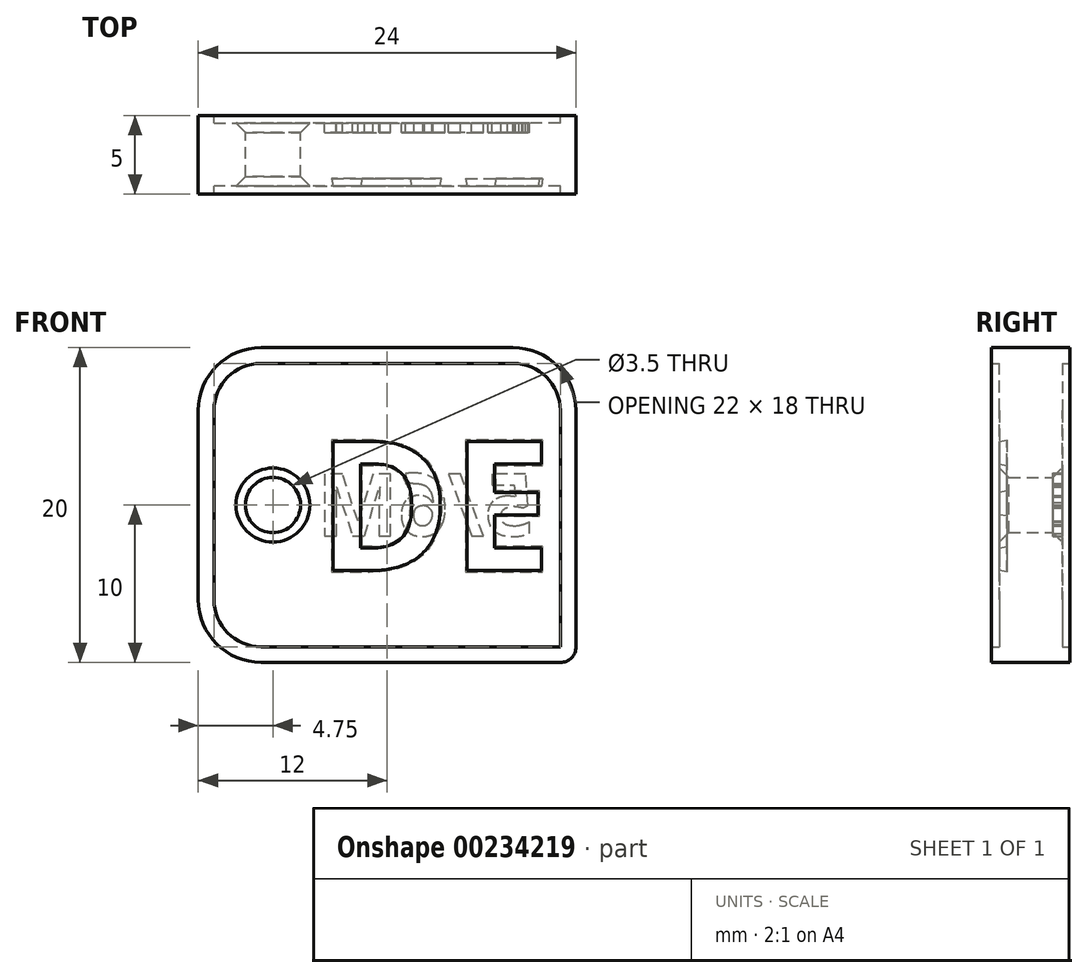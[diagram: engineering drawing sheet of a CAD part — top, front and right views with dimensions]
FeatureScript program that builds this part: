
annotation { "Feature Type Name" : "Feature", "Feature Type Description" : "" }
export const myFeature = defineFeature(function(context is Context, id is Id, definition is map)
    precondition{}
    {
        {
            var Q0;
            Q0=qCreatedBy(makeId("Front.planeOp"),FACE);
            var sketch = newSketch(context, id + "F0", { "sketchPlane" : qUnion([Q0])});
            skLineSegment(sketch, "E0.bottom", {"start": v(12, -10) * mm, "end": v(-12, -10) * mm});
            skLineSegment(sketch, "E0.top", {"start": v(12, 10) * mm, "end": v(-12, 10) * mm});
            skLineSegment(sketch, "E0.left", {"start": v(12, -10) * mm, "end": v(12, 10) * mm});
            skLineSegment(sketch, "E0.right", {"start": v(-12, -10) * mm, "end": v(-12, 10) * mm});
            skPoint(sketch, "E0.middle", {"position": v(0, 0) * mm});
            skCircle(sketch, "E1", {"center": v(-7.25, 0) * mm, "radius": 1.75 * mm});
            skSolve(sketch);
        }
        {
            var Q0;
            Q0=qSketchRegion(id+"F0",true);
            extrude(context, id + "F1", {"entities" : qUnion([Q0]), "endBound" : BoundingType.SYMMETRIC, "depth" : 4 * mm});
        }
        {
            var Q0;
            Q0=makeQuery(id+"F1.opExtrude","SWEPT_EDGE",EDGE,{"disambiguationData":[OSD([sQuery(id+"F0.wireOp",EDGE,"E0.top"),sQuery(id+"F0.wireOp",EDGE,"E0.right")])]});
            var Q1;
            Q1=makeQuery(id+"F1.opExtrude","SWEPT_EDGE",EDGE,{"disambiguationData":[OSD([sQuery(id+"F0.wireOp",EDGE,"E0.top"),sQuery(id+"F0.wireOp",EDGE,"E0.left")])]});
            var Q2;
            Q2=makeQuery(id+"F1.opExtrude","SWEPT_EDGE",EDGE,{"disambiguationData":[OSD([sQuery(id+"F0.wireOp",EDGE,"E0.bottom"),sQuery(id+"F0.wireOp",EDGE,"E0.right")])]});
            fillet(context, id + "F2", {"entities" : qUnion([Q0, Q1, Q2]), "radius" : 4 * mm, "tangentPropagation" : true, "allowEdgeOverflow" : false});
        }
        {
            var Q0;
            Q0=makeQuery(id+"F1.opExtrude","SWEPT_EDGE",EDGE,{"disambiguationData":[OSD([sQuery(id+"F0.wireOp",EDGE,"E0.bottom"),sQuery(id+"F0.wireOp",EDGE,"E0.left")])]});
            fillet(context, id + "F3", {"entities" : qUnion([Q0]), "radius" : 1 * mm, "tangentPropagation" : true, "allowEdgeOverflow" : false});
        }
        {
            var Q0;
            Q0=qCreatedBy(makeId("Front.planeOp"),FACE);
            var sketch = newSketch(context, id + "F4", { "sketchPlane" : qUnion([Q0])});
            skArc(sketch, "E2.0", {"start": v(-11, -6) * mm, "mid": v(-10.12, -8.12) * mm, "end": v(-8, -9) * mm});
            skLineSegment(sketch, "E2.1", {"start": v(-11, 6) * mm, "end": v(-11, -6) * mm});
            skLineSegment(sketch, "E2.2", {"start": v(11, -9) * mm, "end": v(11, 6) * mm});
            skArc(sketch, "E2.3", {"start": v(11, 6) * mm, "mid": v(10.12, 8.12) * mm, "end": v(8, 9) * mm});
            skLineSegment(sketch, "E2.4", {"start": v(8, 9) * mm, "end": v(-8, 9) * mm});
            skLineSegment(sketch, "E2.5", {"start": v(-8, -9) * mm, "end": v(11, -9) * mm});
            skArc(sketch, "E2.6", {"start": v(-8, 9) * mm, "mid": v(-10.12, 8.12) * mm, "end": v(-11, 6) * mm});
            skArc(sketch, "E3.0", {"start": v(-12, -6) * mm, "mid": v(-10.83, -8.83) * mm, "end": v(-8, -10) * mm});
            skLineSegment(sketch, "E3.1", {"start": v(-12, 6) * mm, "end": v(-12, -6) * mm});
            skLineSegment(sketch, "E3.2", {"start": v(-8, -10) * mm, "end": v(11, -10) * mm});
            skArc(sketch, "E3.3", {"start": v(-8, 10) * mm, "mid": v(-10.83, 8.83) * mm, "end": v(-12, 6) * mm});
            skArc(sketch, "E3.4", {"start": v(11, -10) * mm, "mid": v(11.7, -9.7) * mm, "end": v(12, -9) * mm});
            skLineSegment(sketch, "E3.5", {"start": v(12, -9) * mm, "end": v(12, 6) * mm});
            skArc(sketch, "E3.6", {"start": v(12, 6) * mm, "mid": v(10.83, 8.83) * mm, "end": v(8, 10) * mm});
            skLineSegment(sketch, "E3.7", {"start": v(8, 10) * mm, "end": v(-8, 10) * mm});
            skSolve(sketch);
        }
        {
            var Q0;
            Q0=qSketchRegion(id+"F4",true);
            extrude(context, id + "F5", {"entities" : qUnion([Q0]), "operationType" : NewBodyOperationType.ADD, "endBound" : BoundingType.SYMMETRIC, "depth" : 5 * mm});
        }
        {
            var Q0;
            Q0=makeQuery(id+"F1.opExtrude","CAP_FACE",FACE,{"disambiguationData":[OSD([sQuery(id+"F0.wireOp",EDGE,"E0.bottom"),sQuery(id+"F0.wireOp",EDGE,"E0.top"),sQuery(id+"F0.wireOp",EDGE,"E0.left"),sQuery(id+"F0.wireOp",EDGE,"E0.right"),sQuery(id+"F0.wireOp",EDGE,"E1")])],"isStart":false});
            var sketch = newSketch(context, id + "F6", { "sketchPlane" : qUnion([Q0])});
            skText(sketch, "E4", { "text": "DE", "fontName": "OpenSans-Bold.ttf"});
            const initialGuessF6  = {"E4": [-0.00446, -0.00417, 1, 0, 0.00827]};
            skSetInitialGuess(sketch, initialGuessF6);
            skSolve(sketch);
        }
        {
            var Q0;
            Q0=qSketchRegion(id+"F6",true);
            extrude(context, id + "F7", {"entities" : qUnion([Q0]), "operationType" : NewBodyOperationType.REMOVE, "oppositeDirection" : true, "depth" : 0.5 * mm, "hasDraft" : true, "draftAngle" : 10 * degree});
        }
        {
            var Q0;
            Q0=makeQuery(id+"F1.opExtrude","CAP_EDGE",EDGE,{"disambiguationData":[OSD([sQuery(id+"F0.wireOp",EDGE,"E1")])],"isStart":false});
            var Q1;
            Q1=makeQuery(id+"F1.opExtrude","CAP_EDGE",EDGE,{"disambiguationData":[OSD([sQuery(id+"F0.wireOp",EDGE,"E1")])],"isStart":true});
            chamfer(context, id + "F8", {"entities" : qUnion([Q0, Q1]), "width" : .6 * mm, "tangentPropagation" : true});
        }
        {
            var Q0;
            Q0=makeQuery(id+"F1.opExtrude","CAP_FACE",FACE,{"disambiguationData":[OSD([sQuery(id+"F0.wireOp",EDGE,"E0.bottom"),sQuery(id+"F0.wireOp",EDGE,"E0.top"),sQuery(id+"F0.wireOp",EDGE,"E0.left"),sQuery(id+"F0.wireOp",EDGE,"E0.right"),sQuery(id+"F0.wireOp",EDGE,"E1")])],"isStart":true});
            var sketch = newSketch(context, id + "F9", { "sketchPlane" : qUnion([Q0])});
            skText(sketch, "E5", { "text": "5/6M", "fontName": "OpenSans-Bold.ttf"});
            const initialGuessF9  = {"E5": [-0.0093, -0.00195, 1, 0, 0.00397]};
            skSetInitialGuess(sketch, initialGuessF9);
            skSolve(sketch);
        }
        {
            var Q0;
            Q0=qSketchRegion(id+"F9",true);
            extrude(context, id + "F10", {"entities" : qUnion([Q0]), "operationType" : NewBodyOperationType.REMOVE, "oppositeDirection" : true, "depth" : 0.6 * mm});
        }
    });
